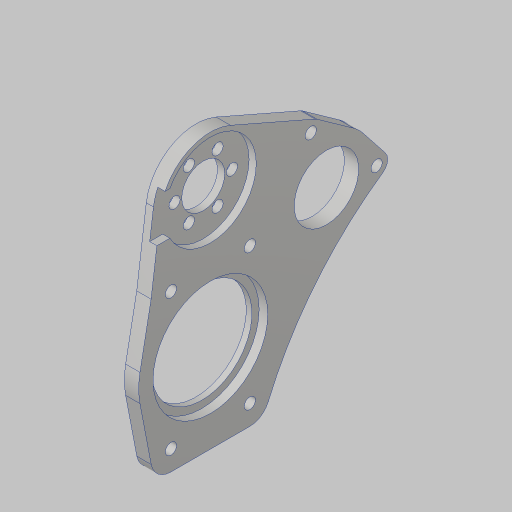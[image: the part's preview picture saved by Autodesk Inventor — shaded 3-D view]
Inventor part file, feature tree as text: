
AUTODESK INVENTOR PART (.ipt)
format: ipt  version: 2023.5 (Build 275446000, 446)  size: 255,488 bytes
history: native  units: in
note: dims shown in document units (in); Inventor stores cm internally (conversion verified against a paired STEP export)
features: sketch x5, extrude x4, hole x2, projected_geometry x1
ambient origin geometry x8: Origin, YZ Plane, XZ Plane, XY Plane, X Axis, Y Axis, Z Axis, Center Point
bodies: Solid1 (feature_tree)
feature tree (12):
  sketch  "Sketch1"  dims[d0=3.0in d1=2.2in]
  sketch  "Sketch2"  dims[d2=3.0in d3=2.375in]
  extrude  "Extrusion1"  Depth=2.2in
  hole  "Motor Mount Holes"  [1 undecoded]
  hole  "Hole3"  [1 undecoded]
  extrude  "Extrusion2"  Depth=0.201in
  extrude  "Extrusion3"  Depth=1.0in
  extrude  "Extrusion4"  Depth=0.875in TaperAngle=360.0deg
  sketch  "Sketch3"  dims[d4=1.375in d5=0.201in]
  sketch  "Sketch4"  dims[d6=0.201in d7=0.201in]
  sketch  "Sketch5"  dims[d8=0.201in d9=1.0in d12=2.3622in d14=360.0deg d16=1.125in d17=2.246in d19=2.0in d20=0.75in d23=0.25in d24=0.25in d25=0.0in d33=0.196in d34=0.75in d35=0.375in d36=0.25in d37=0.5635in d38=1.0in d39=0.8108in d41=1.1811in d43=360.0deg d45=0.375in d46=0.385in d47=0.375in d49=0.196in d50=0.75in d51=0.385in d52=0.25in d53=0.5635in d54=1.0in d55=0.8108in d56=2.0in d57=0.25in d58=1.75in d60=3.0in d61=1.6in d62=0.125in d63=0.0in d65=2.362in d66=0.25in d68=0.75in d69=0.375in d70=0.125in d71=0.0in d72=1.75in d73=0.1in d74=0.0in d75=0.6in d76=2.0in d77=0.875in d78=1.75in]
  projected_geometry  "Project Cut Edges1"
note: 2 required parameter values undecoded (feature->parameter linkage not recoverable at this tier; creation-order binding heuristic only, values carry confidence <= 0.55)
